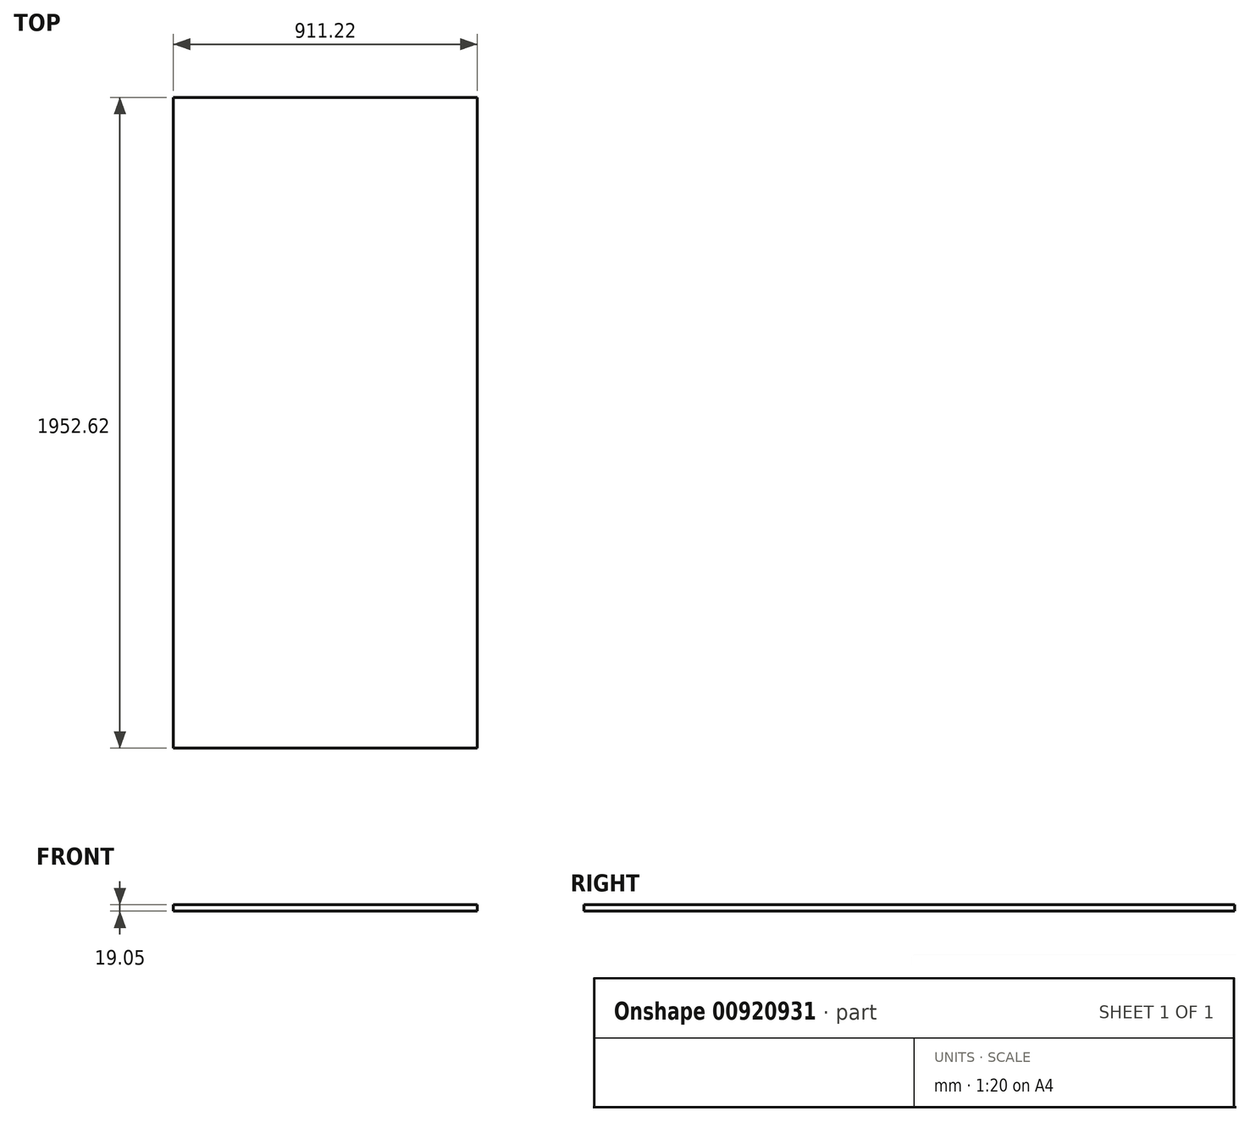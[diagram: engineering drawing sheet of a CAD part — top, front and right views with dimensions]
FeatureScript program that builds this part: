
annotation { "Feature Type Name" : "Feature", "Feature Type Description" : "" }
export const myFeature = defineFeature(function(context is Context, id is Id, definition is map)
    precondition{}
    {
        {
            assignVariable(context, id + "F0", {"name" : "pbrdThick", "anyValue" : 19.05 * mm});
        }
        {
            var Q0;
            Q0=qCreatedBy(makeId("Top.planeOp"),FACE);
            var sketch = newSketch(context, id + "F1", { "sketchPlane" : qUnion([Q0])});
            skPoint(sketch, "E0", {"position": v(-456.58, 975.35) * mm});
            skPoint(sketch, "E1", {"position": v(454.65, 975.35) * mm});
            skPoint(sketch, "E2", {"position": v(-456.57, -977.27) * mm});
            skPoint(sketch, "E3", {"position": v(454.65, -977.27) * mm});
            skLineSegment(sketch, "E4", {"start": v(-456.57, -977.27) * mm, "end": v(454.65, -977.27) * mm});
            skLineSegment(sketch, "E5", {"start": v(454.65, 975.35) * mm, "end": v(454.65, -977.27) * mm});
            skLineSegment(sketch, "E6", {"start": v(454.65, 975.35) * mm, "end": v(-456.58, 975.35) * mm});
            skLineSegment(sketch, "E7", {"start": v(-456.57, 975.35) * mm, "end": v(-456.57, -977.27) * mm});
            skSolve(sketch);
        }
        {
            var Q0;
            Q0 = qSketchRegion(id + "F1", true);
            extrude(context, id + "F2", {"entities" : qUnion([Q0]), "depth" : getVariable(context, 'pbrdThick'), "offsetDistance" : 25 * mm});
        }
    });
